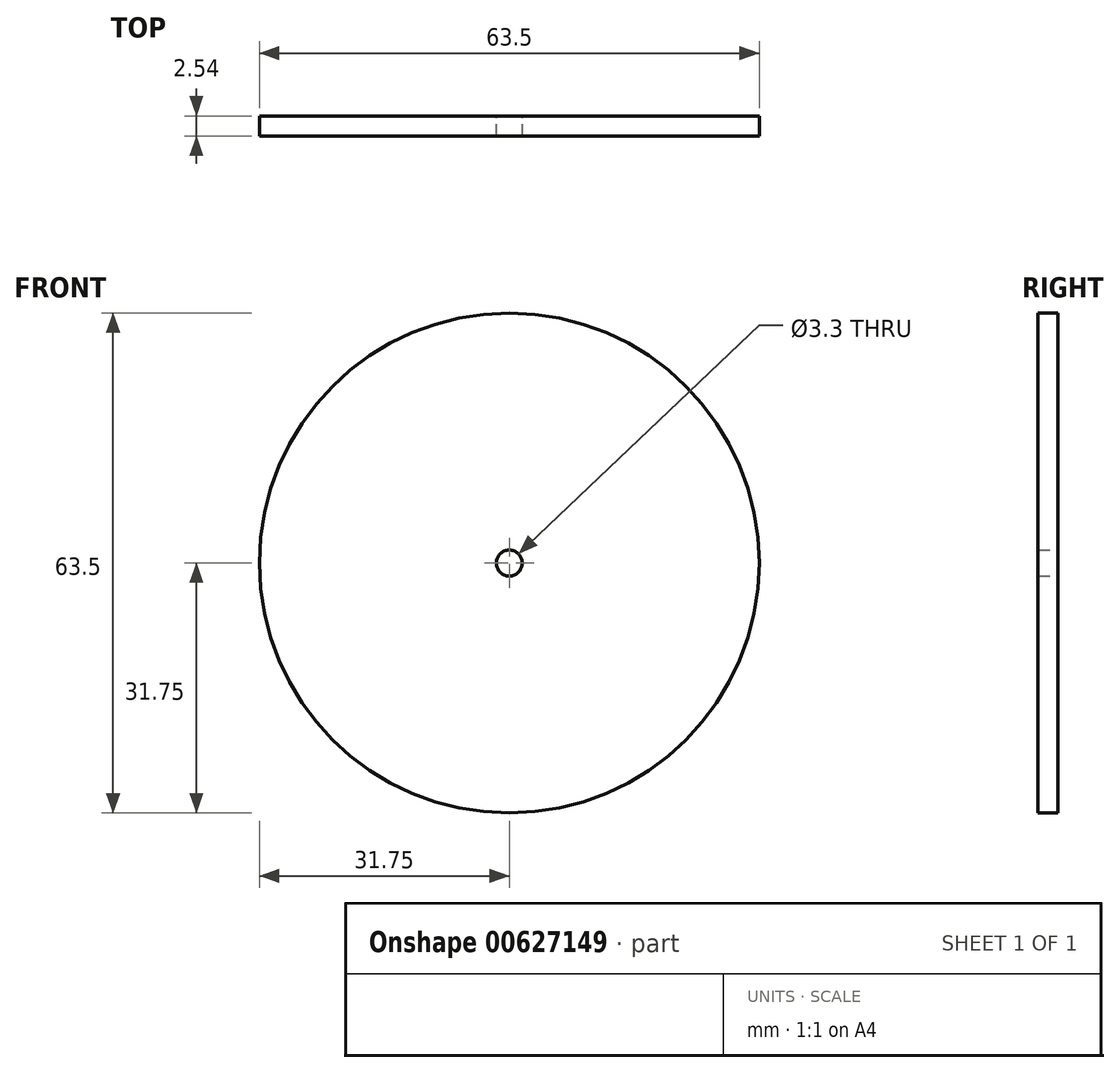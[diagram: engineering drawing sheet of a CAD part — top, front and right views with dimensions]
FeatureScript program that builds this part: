
annotation { "Feature Type Name" : "Feature", "Feature Type Description" : "" }
export const myFeature = defineFeature(function(context is Context, id is Id, definition is map)
    precondition{}
    {
        {
            var Q0;
            Q0=qCreatedBy(makeId("Front.planeOp"),FACE);
            var sketch = newSketch(context, id + "F0", { "sketchPlane" : qUnion([Q0])});
            skCircle(sketch, "E0", {"center": v(0, 0) * mm, "radius": 31.75 * mm});
            skCircle(sketch, "E1", {"center": v(0, 0) * mm, "radius": 1.65 * mm});
            skSolve(sketch);
        }
        {
            var Q0;
            Q0 = qSketchRegion(id + "F0", true);
            extrude(context, id + "F1", {"entities" : qUnion([Q0]), "depth" : 2.54 * mm, "offsetDistance" : 25.4 * mm});
        }
    });
